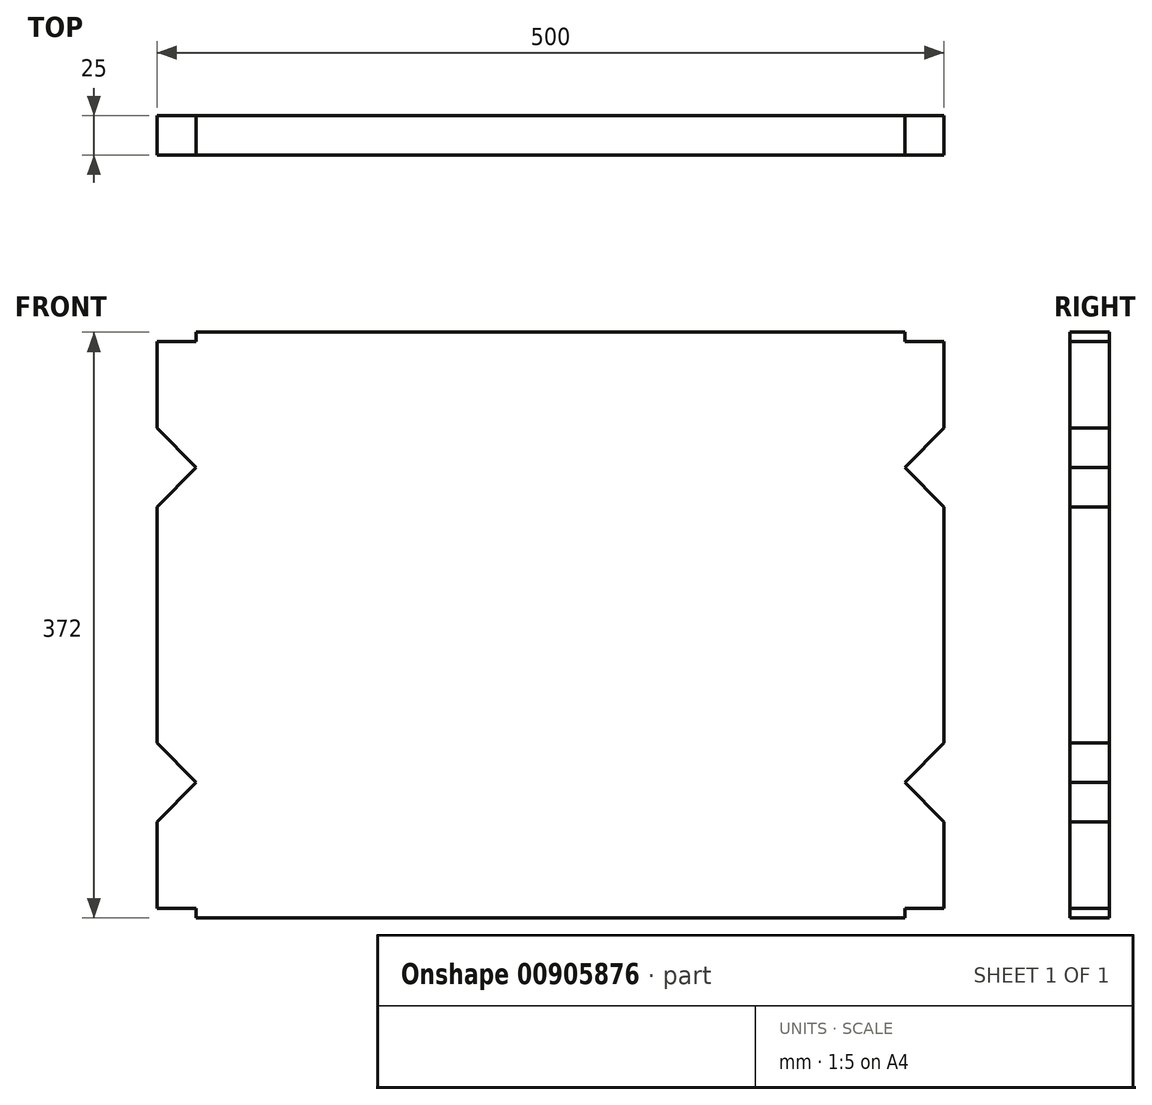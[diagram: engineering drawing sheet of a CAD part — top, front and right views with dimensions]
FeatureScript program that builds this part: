
annotation { "Feature Type Name" : "Feature", "Feature Type Description" : "" }
export const myFeature = defineFeature(function(context is Context, id is Id, definition is map)
    precondition{}
    {
        {
            var Q0;
            Q0=qCreatedBy(makeId("Front.planeOp"),FACE);
            var sketch = newSketch(context, id + "F0", { "sketchPlane" : qUnion([Q0])});
            skLineSegment(sketch, "E0.bottom", {"start": v(225, -186) * mm, "end": v(-225, -186) * mm});
            skLineSegment(sketch, "E0.top", {"start": v(225, 186) * mm, "end": v(-225, 186) * mm});
            skLineSegment(sketch, "E0.left", {"start": v(250, -180) * mm, "end": v(250, -125) * mm});
            skLineSegment(sketch, "E0.right", {"start": v(-250, -180) * mm, "end": v(-250, -125) * mm});
            skPoint(sketch, "E0.middle", {"position": v(0, 0) * mm});
            skLineSegment(sketch, "E1.top", {"start": v(-250, 180) * mm, "end": v(-225, 180) * mm});
            skLineSegment(sketch, "E1.right", {"start": v(-225, 186) * mm, "end": v(-225, 180) * mm});
            skPoint(sketch, "E2.oppositeSnap0", {"position": v(-237.5, 180) * mm});
            skLineSegment(sketch, "E2.top", {"start": v(250, 180) * mm, "end": v(225, 180) * mm});
            skLineSegment(sketch, "E2.right", {"start": v(225, 186) * mm, "end": v(225, 180) * mm});
            skLineSegment(sketch, "E3.top", {"start": v(-250, -180) * mm, "end": v(-225, -180) * mm});
            skLineSegment(sketch, "E3.right", {"start": v(-225, -186) * mm, "end": v(-225, -180) * mm});
            skLineSegment(sketch, "E4.top", {"start": v(250, -180) * mm, "end": v(225, -180) * mm});
            skLineSegment(sketch, "E4.right", {"start": v(225, -186) * mm, "end": v(225, -180) * mm});
            skLineSegment(sketch, "E5", {"start": v(-225, -100) * mm, "end": v(-250, -125) * mm});
            skLineSegment(sketch, "E6", {"start": v(-250, -75) * mm, "end": v(-225, -100) * mm});
            skLineSegment(sketch, "E7.trimOffspring", {"start": v(-250, -75) * mm, "end": v(-250, 75) * mm});
            skLineSegment(sketch, "E8", {"start": v(-250, 180) * mm, "end": v(-250, 151.43) * mm});
            skLineSegment(sketch, "E9.trimOffspring", {"start": v(-250, 150) * mm, "end": v(-250, 180) * mm});
            skLineSegment(sketch, "E10", {"start": v(225, -100) * mm, "end": v(250, -75) * mm});
            skLineSegment(sketch, "E11", {"start": v(250, -125) * mm, "end": v(225, -100) * mm});
            skLineSegment(sketch, "E12.trimOffspring", {"start": v(250, -75) * mm, "end": v(250, 75) * mm});
            skLineSegment(sketch, "E13", {"start": v(225, 100) * mm, "end": v(250, 125) * mm});
            skLineSegment(sketch, "E14", {"start": v(250, 75) * mm, "end": v(225, 100) * mm});
            skLineSegment(sketch, "E15.trimOffspring", {"start": v(250, 125) * mm, "end": v(250, 180) * mm});
            skLineSegment(sketch, "E16", {"start": v(-250, 151.43) * mm, "end": v(-250, 125) * mm});
            skLineSegment(sketch, "E17", {"start": v(-225, 100) * mm, "end": v(-250, 125) * mm});
            skLineSegment(sketch, "E18", {"start": v(-250, 75) * mm, "end": v(-225, 100) * mm});
            skSolve(sketch);
        }
        {
            var Q0;
            Q0=makeQuery(id+"F0.imprint","IMPRINT",FACE,{"disambiguationData":[TD([[makeQuery(id+"F0.imprint","IMPRINT",EDGE,{"derivedFrom":sQuery(id+"F0.wireOp",EDGE,"E0.bottom")}),-1.0]])]});
            extrude(context, id + "F1", {"entities" : qUnion([Q0]), "depth" : 25 * mm, "offsetDistance" : 25 * mm});
        }
    });
